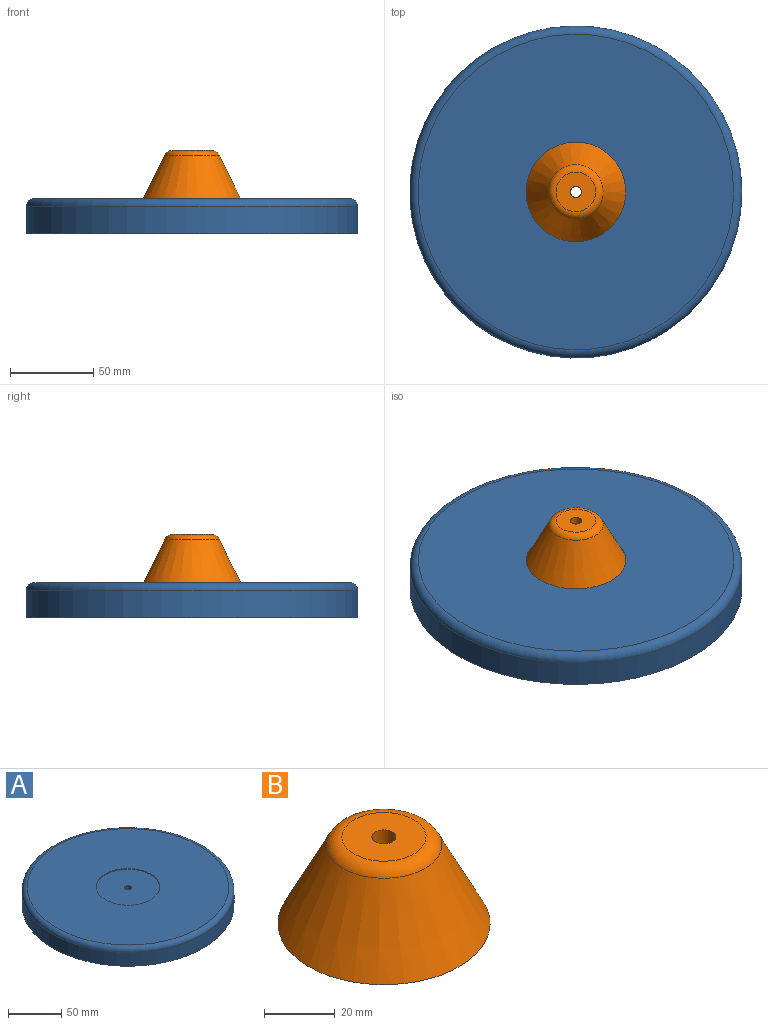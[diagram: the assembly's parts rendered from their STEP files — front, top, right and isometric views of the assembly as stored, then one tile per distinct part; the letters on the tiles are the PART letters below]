
ASSEMBLY  parts=2 mates=1
PART A: 9 faces, bbox 216.5x216.5x21 mm
  f0: plane 190x190mm, normal (0,0,1), area 25525.4mm2, adj f1,f8
  f1: cylinder r=30mm len=60mm, axis (0,0,1), area 188.5mm2, adj f0,f2
  f2: plane 60x60mm, normal (0,0,1), area 2791.1mm2, adj f1,f3
  f3: cylinder r=3.4mm len=6.8mm, axis (0,0,1), area 85.5mm2, adj f2,f4
  f4: plane 190x190mm, normal (0,0,-1), area 28316.6mm2, adj f3,f5
  f5: cylinder r=95mm len=190mm, axis (0,0,1), area 9550.4mm2, adj f4,f6
  f6: plane 200x200mm, normal (0,0,-1), area 3063.1mm2, adj f5,f7
  f7: cylinder r=100mm len=200mm, axis (0,0,1), area 10053.1mm2, adj f6,f8
  f8: torus R=95mm, axis (0,0,1), area 4845.1mm2, adj f0,f7
PART B: 7 faces, bbox 60x60x30 mm
  f0: cone r=24mm half-angle=26.6deg, axis (0,0,-1), area 3117.3mm2, adj f1,f5
  f1: plane 60x60mm, normal (0,0,-1), area 1017.9mm2, adj f0,f2
  f2: cone r=30mm half-angle=26.6deg, axis (0,0,-1), area 4437.1mm2, adj f1,f6
  f3: plane 23.82x23.82mm, normal (0,0,1), area 409.3mm2, adj f4,f6
  f4: cylinder r=3.4mm len=6.8mm, axis (0,0,-1), area 106.8mm2, adj f3,f5
  f5: plane 23x23mm, normal (0,0,-1), area 379.2mm2, adj f0,f4
  f6: torus R=11.91mm, axis (0,0,1), area 501.1mm2, adj f2,f3
PLACE A t=(54.11,59.39,33.56)mm
PLACE B t=(54.11,59.39,62.56)mm
MATE planar A.f1 <-> B.f0  axis (0,0,1) through (50.71,59.39,32.56)mm
